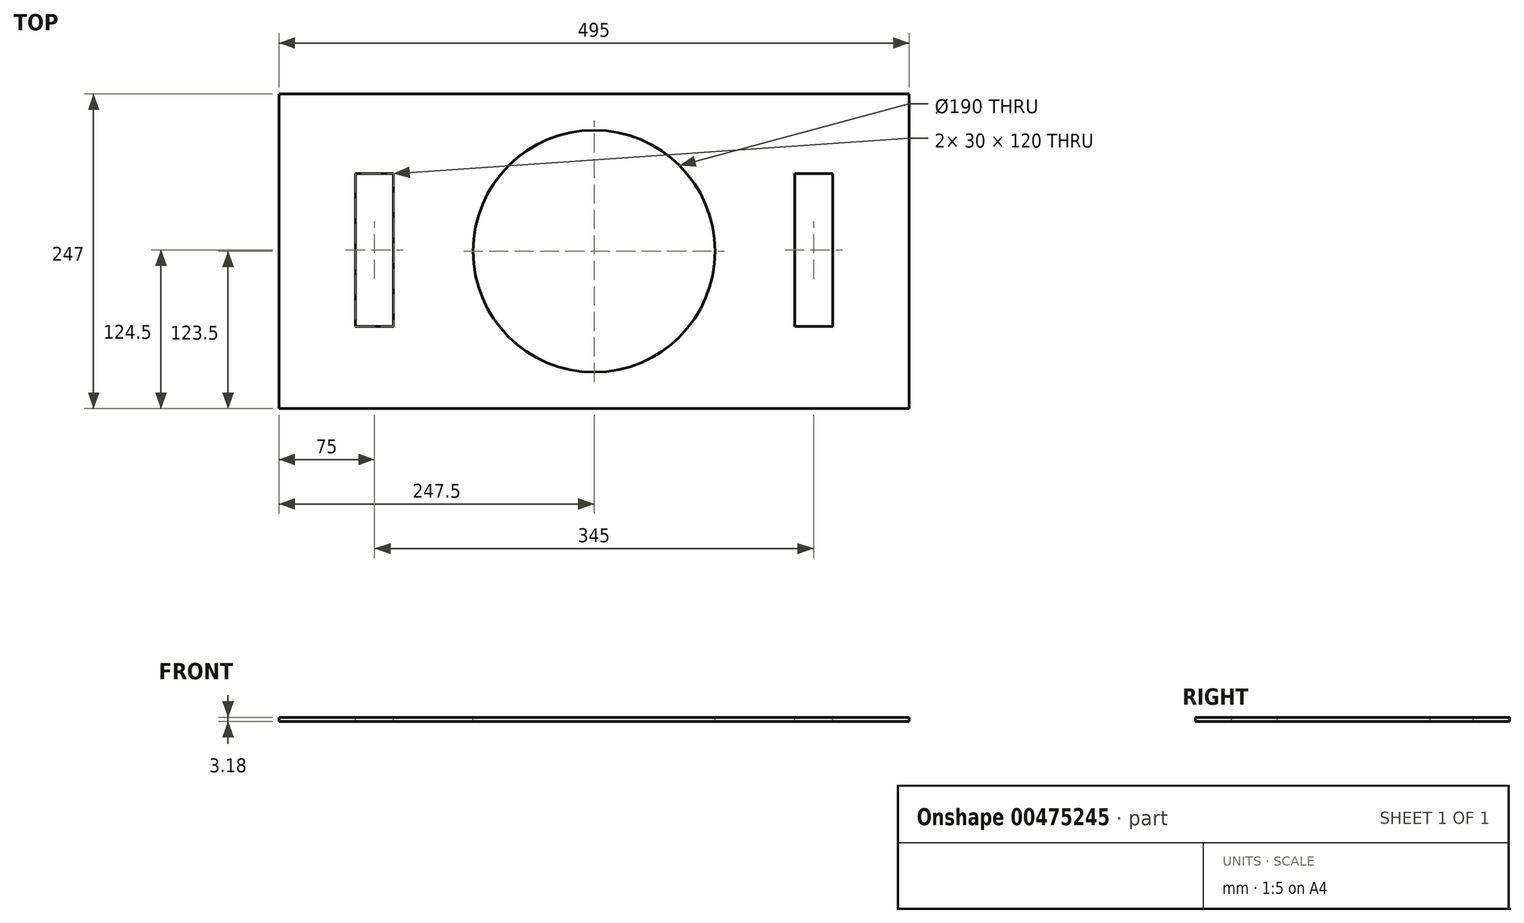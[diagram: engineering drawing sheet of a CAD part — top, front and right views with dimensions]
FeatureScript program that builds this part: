
annotation { "Feature Type Name" : "Feature", "Feature Type Description" : "" }
export const myFeature = defineFeature(function(context is Context, id is Id, definition is map)
    precondition{}
    {
        {
            var Q0;
            Q0=qCreatedBy(makeId("Top.planeOp"),FACE);
            var sketch = newSketch(context, id + "F0", { "sketchPlane" : qUnion([Q0])});
            skLineSegment(sketch, "E0.bottom", {"start": v(-247.5, 123.5) * mm, "end": v(247.5, 123.5) * mm});
            skLineSegment(sketch, "E0.top", {"start": v(-247.5, -123.5) * mm, "end": v(247.5, -123.5) * mm});
            skLineSegment(sketch, "E0.left", {"start": v(-247.5, 123.5) * mm, "end": v(-247.5, -123.5) * mm});
            skLineSegment(sketch, "E0.right", {"start": v(247.5, 123.5) * mm, "end": v(247.5, -123.5) * mm});
            skLineSegment(sketch, "E1", {"start": v(0, -123.5) * mm, "end": v(0, 123.5) * mm});
            skLineSegment(sketch, "E2", {"start": v(-247.5, 0) * mm, "end": v(247.5, 0) * mm});
            skCircle(sketch, "E3", {"center": v(0, 0) * mm, "radius": 95 * mm});
            skLineSegment(sketch, "E4", {"start": v(-187.5, 61) * mm, "end": v(-187.5, -59) * mm});
            skLineSegment(sketch, "E5", {"start": v(-157.5, -59) * mm, "end": v(-157.5, 61) * mm});
            skLineSegment(sketch, "E6", {"start": v(157.5, 61) * mm, "end": v(157.5, -59) * mm});
            skLineSegment(sketch, "E7", {"start": v(187.5, -59) * mm, "end": v(187.5, 61) * mm});
            skLineSegment(sketch, "E8", {"start": v(-187.5, 61) * mm, "end": v(-157.5, 61) * mm});
            skLineSegment(sketch, "E9", {"start": v(-157.5, -59) * mm, "end": v(-187.5, -59) * mm});
            skLineSegment(sketch, "E10", {"start": v(157.5, -59) * mm, "end": v(187.5, -59) * mm});
            skLineSegment(sketch, "E11", {"start": v(157.5, 61) * mm, "end": v(187.5, 61) * mm});
            skSolve(sketch);
        }
        {
            var Q0;
            Q0 = qSketchRegion(id + "F0", true);
            extrude(context, id + "F1", {"entities" : qUnion([Q0]), "oppositeDirection" : true, "depth" : 3.17 * mm});
        }
    });
